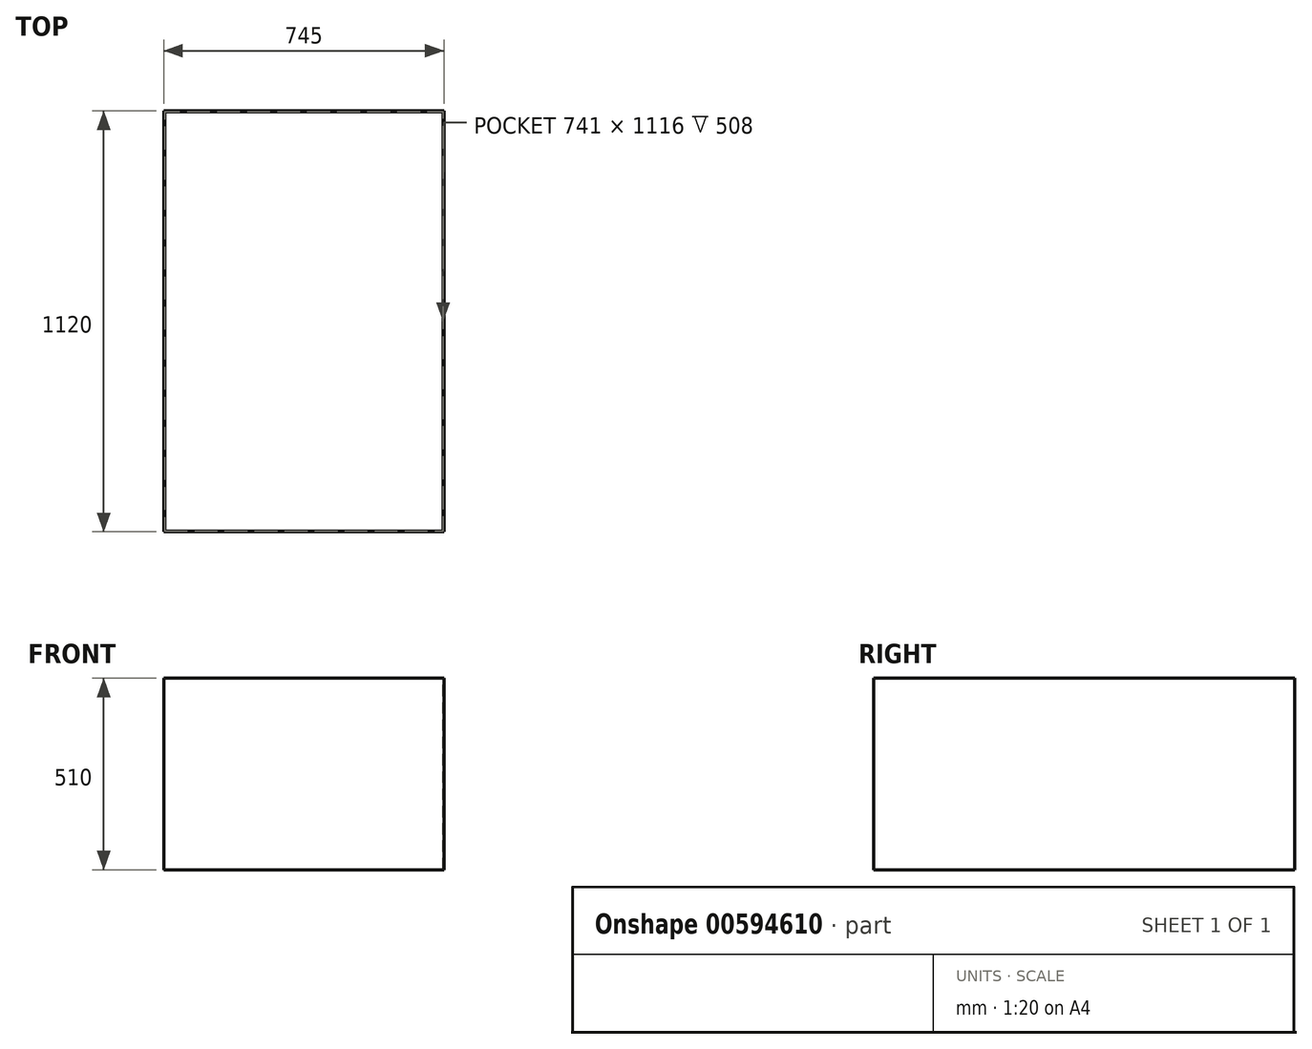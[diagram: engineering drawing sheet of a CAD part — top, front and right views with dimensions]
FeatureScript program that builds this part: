
annotation { "Feature Type Name" : "Feature", "Feature Type Description" : "" }
export const myFeature = defineFeature(function(context is Context, id is Id, definition is map)
    precondition{}
    {
        {
            var Q0;
            Q0=qCreatedBy(makeId("Top.planeOp"),FACE);
            var sketch = newSketch(context, id + "F0", { "sketchPlane" : qUnion([Q0])});
            skLineSegment(sketch, "E0.bottom", {"start": v(0, 0) * mm, "end": v(745, 0) * mm});
            skLineSegment(sketch, "E0.top", {"start": v(0, 1120) * mm, "end": v(745, 1120) * mm});
            skLineSegment(sketch, "E0.left", {"start": v(0, 0) * mm, "end": v(0, 1120) * mm});
            skLineSegment(sketch, "E0.right", {"start": v(745, 0) * mm, "end": v(745, 1120) * mm});
            skSolve(sketch);
        }
        {
            var Q0;
            Q0 = qSketchRegion(id + "F0", true);
            extrude(context, id + "F1", {"entities" : qUnion([Q0]), "depth" : 510 * mm, "offsetDistance" : 25 * mm});
        }
        {
            var Q0;
            Q0=makeQuery(id+"F1.opExtrude","CAP_FACE",FACE,{"disambiguationData":[OSD([sQuery(id+"F0.wireOp",EDGE,"E0.bottom"),sQuery(id+"F0.wireOp",EDGE,"E0.top"),sQuery(id+"F0.wireOp",EDGE,"E0.left"),sQuery(id+"F0.wireOp",EDGE,"E0.right")])],"isStart":false});
            var sketch = newSketch(context, id + "F2", { "sketchPlane" : qUnion([Q0])});
            skLineSegment(sketch, "E1.bottom", {"start": v(2, 2) * mm, "end": v(743, 2) * mm});
            skLineSegment(sketch, "E1.top", {"start": v(2, 1118) * mm, "end": v(743, 1118) * mm});
            skLineSegment(sketch, "E1.left", {"start": v(2, 2) * mm, "end": v(2, 1118) * mm});
            skLineSegment(sketch, "E1.right", {"start": v(743, 2) * mm, "end": v(743, 1118) * mm});
            skSolve(sketch);
        }
        {
            var Q0;
            Q0=makeQuery(id+"F2.imprint","IMPRINT",FACE,{"disambiguationData":[TD([[makeQuery(id+"F2.imprint","IMPRINT",EDGE,{"derivedFrom":sQuery(id+"F2.wireOp",EDGE,"E1.bottom")}),1.0]])]});
            extrude(context, id + "F3", {"entities" : qUnion([Q0]), "operationType" : NewBodyOperationType.REMOVE, "oppositeDirection" : true, "depth" : (510 - 2) * mm, "offsetDistance" : 25 * mm});
        }
    });
